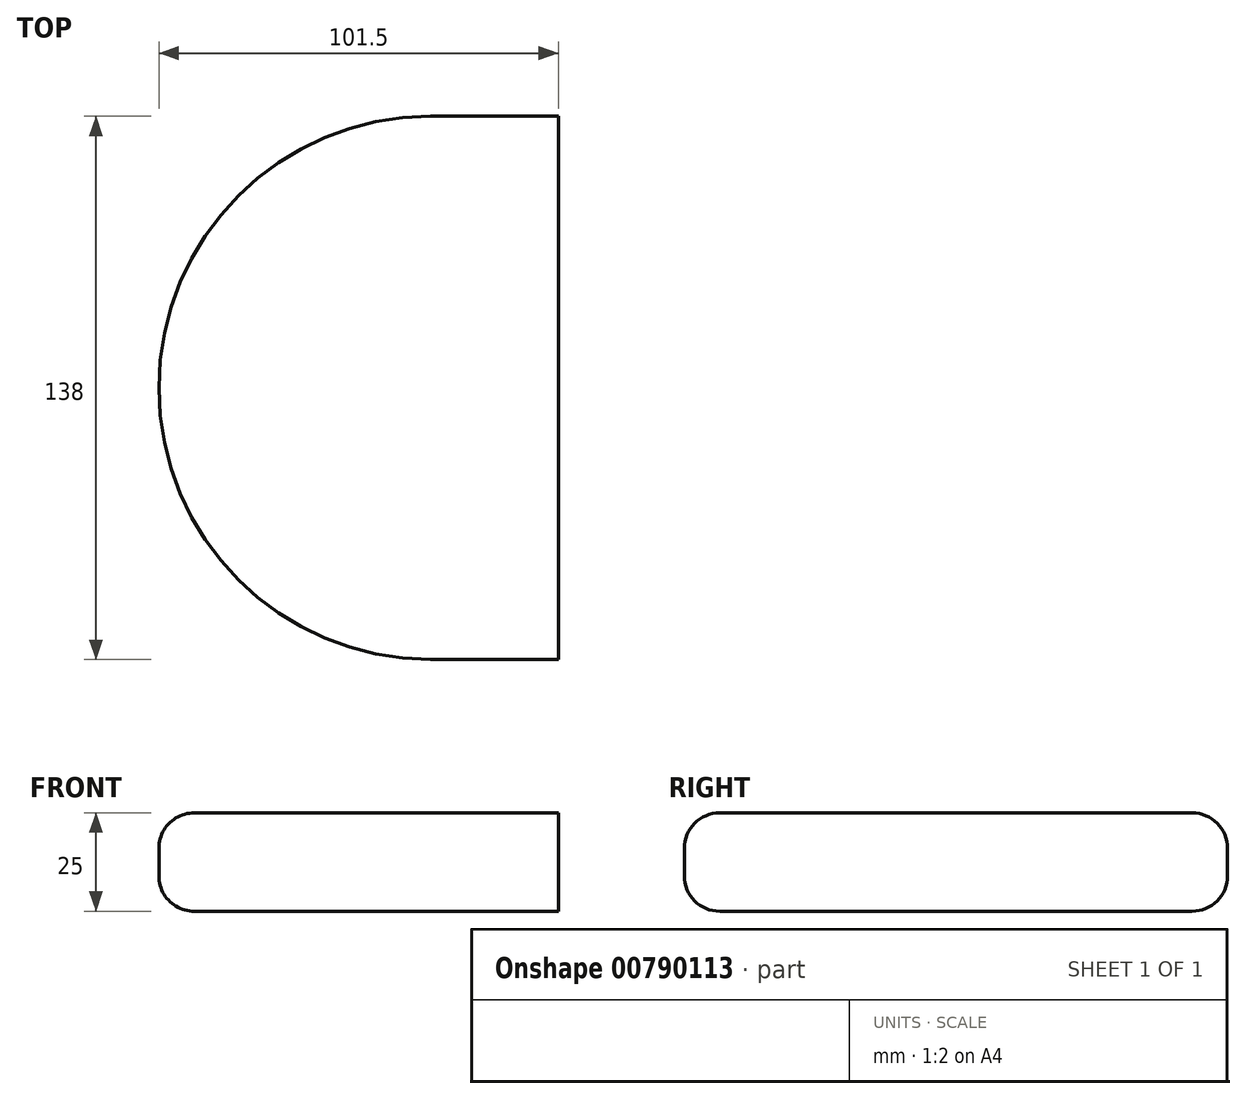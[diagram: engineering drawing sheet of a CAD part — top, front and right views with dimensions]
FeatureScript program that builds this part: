
annotation { "Feature Type Name" : "Feature", "Feature Type Description" : "" }
export const myFeature = defineFeature(function(context is Context, id is Id, definition is map)
    precondition{}
    {
        {
            var Q0;
            Q0=qCreatedBy(makeId("Top.planeOp"),FACE);
            var sketch = newSketch(context, id + "F0", { "sketchPlane" : qUnion([Q0])});
            skArc(sketch, "E0", {"start": v(0, 69) * mm, "mid": v(69, 0) * mm, "end": v(0, -69) * mm});
            skArc(sketch, "E1", {"start": v(-32.5, 69) * mm, "mid": v(-101.5, 0) * mm, "end": v(-32.5, -69) * mm});
            skLineSegment(sketch, "E2", {"start": v(0, 69) * mm, "end": v(0, -69) * mm});
            skLineSegment(sketch, "E3", {"start": v(0, 69) * mm, "end": v(-32.5, 69) * mm});
            skLineSegment(sketch, "E4", {"start": v(-32.5, 69) * mm, "end": v(-32.5, -69) * mm});
            skLineSegment(sketch, "E5", {"start": v(0, -69) * mm, "end": v(-32.5, -69) * mm});
            skPoint(sketch, "E6", {"position": v(-17.2, 57.5) * mm});
            skSolve(sketch);
        }
        {
            var Q0;
            Q0=makeQuery(id+"F0.imprint","IMPRINT",FACE,{"disambiguationData":[TD([[makeQuery(id+"F0.imprint","IMPRINT",EDGE,{"derivedFrom":sQuery(id+"F0.wireOp",EDGE,"E1")}),1.0]])]});
            var Q1;
            Q1=makeQuery(id+"F0.imprint","IMPRINT",FACE,{"disambiguationData":[TD([[makeQuery(id+"F0.imprint","IMPRINT",EDGE,{"derivedFrom":sQuery(id+"F0.wireOp",EDGE,"E2")}),-1.0]])]});
            var Q2;
            Q2=makeQuery(id+"F0.imprint","IMPRINT",FACE,{"disambiguationData":[TD([[makeQuery(id+"F0.imprint","IMPRINT",EDGE,{"derivedFrom":sQuery(id+"F0.wireOp",EDGE,"E0")}),-1.0]])]});
            extrude(context, id + "F1", {"entities" : qUnion([Q0, Q1, Q2]), "depth" : 25 * mm, "offsetDistance" : 25 * mm});
        }
        {
            var Q0;
            Q0=makeQuery(id+"F1.opExtrude","CAP_EDGE",EDGE,{"disambiguationData":[OSD([sQuery(id+"F0.wireOp",EDGE,"E1")])],"isStart":false});
            var Q1;
            Q1=makeQuery(id+"F1.opExtrude","CAP_EDGE",EDGE,{"disambiguationData":[OSD([sQuery(id+"F0.wireOp",EDGE,"E0")])],"isStart":false});
            var Q2;
            Q2=makeQuery(id+"F1.opExtrude","CAP_EDGE",EDGE,{"disambiguationData":[OSD([sQuery(id+"F0.wireOp",EDGE,"E3")])],"isStart":false});
            var Q3;
            Q3=makeQuery(id+"F1.opExtrude","CAP_EDGE",EDGE,{"disambiguationData":[OSD([sQuery(id+"F0.wireOp",EDGE,"E3")])],"isStart":true});
            var Q4;
            Q4=makeQuery(id+"F1.opExtrude","CAP_EDGE",EDGE,{"disambiguationData":[OSD([sQuery(id+"F0.wireOp",EDGE,"E0")])],"isStart":true});
            var Q5;
            Q5=makeQuery(id+"F1.opExtrude","CAP_EDGE",EDGE,{"disambiguationData":[OSD([sQuery(id+"F0.wireOp",EDGE,"E1")])],"isStart":true});
            var Q6;
            Q6=makeQuery(id+"F1.opExtrude","CAP_EDGE",EDGE,{"disambiguationData":[OSD([sQuery(id+"F0.wireOp",EDGE,"E5")])],"isStart":false});
            var Q7;
            Q7=makeQuery(id+"F1.opExtrude","CAP_EDGE",EDGE,{"disambiguationData":[OSD([sQuery(id+"F0.wireOp",EDGE,"E5")])],"isStart":true});
            fillet(context, id + "F2", {"entities" : qUnion([Q0, Q1, Q2, Q3, Q4, Q5, Q6, Q7]), "radius" : 9 * mm, "tangentPropagation" : true, "allowEdgeOverflow" : false});
        }
    });
